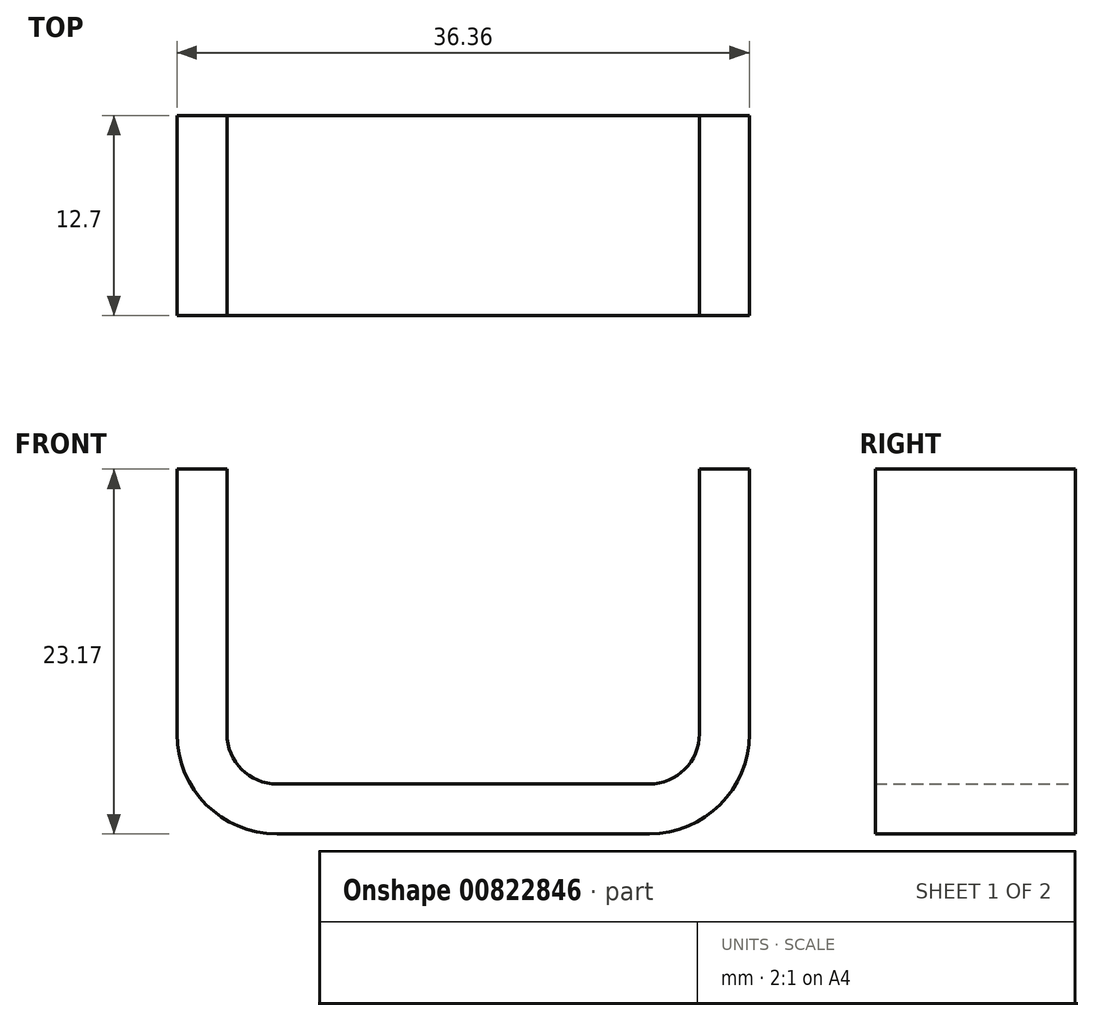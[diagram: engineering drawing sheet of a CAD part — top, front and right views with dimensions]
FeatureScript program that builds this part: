
annotation { "Feature Type Name" : "Feature", "Feature Type Description" : "" }
export const myFeature = defineFeature(function(context is Context, id is Id, definition is map)
    precondition{}
    {
        {
            var Q0;
            Q0=qCreatedBy(makeId("Front.planeOp"),FACE);
            var sketch = newSketch(context, id + "F0", { "sketchPlane" : qUnion([Q0])});
            skLineSegment(sketch, "E0", {"start": v(0, 0) * mm, "end": v(0, 17.47) * mm, "construction": true});
            skLineSegment(sketch, "E1", {"start": v(0, 0) * mm, "end": v(-15, 0) * mm});
            skLineSegment(sketch, "E2", {"start": v(-15, 0) * mm, "end": v(-15, 20) * mm});
            skLineSegment(sketch, "E3.MirrorCS", {"start": v(0, 0) * mm, "end": v(15, 0) * mm});
            skLineSegment(sketch, "E4.MirrorCS", {"start": v(15, 0) * mm, "end": v(15, 20) * mm});
            skLineSegment(sketch, "E5.0", {"start": v(-18.18, -3.18) * mm, "end": v(-18.18, 20) * mm});
            skLineSegment(sketch, "E5.1", {"start": v(0, -3.17) * mm, "end": v(-18.18, -3.18) * mm});
            skLineSegment(sketch, "E5.2", {"start": v(0, -3.17) * mm, "end": v(18.18, -3.17) * mm});
            skLineSegment(sketch, "E5.3", {"start": v(18.18, -3.18) * mm, "end": v(18.18, 20) * mm});
            skLineSegment(sketch, "E6", {"start": v(-18.18, 20) * mm, "end": v(-15, 20) * mm});
            skLineSegment(sketch, "E7", {"start": v(15, 20) * mm, "end": v(18.18, 20) * mm});
            skSolve(sketch);
        }
        {
            var Q0;
            Q0 = qSketchRegion(id + "F0", true);
            extrude(context, id + "F1", {"entities" : qUnion([Q0]), "endBound" : BoundingType.SYMMETRIC, "depth" : 12.7 * mm, "offsetDistance" : 25 * mm});
        }
        {
            var Q0;
            Q0=makeQuery(id+"F1.opExtrude","SWEPT_EDGE",EDGE,{"disambiguationData":[OSD([sQuery(id+"F0.wireOp",EDGE,"E3.MirrorCS"),sQuery(id+"F0.wireOp",EDGE,"E4.MirrorCS")])]});
            var Q1;
            Q1=makeQuery(id+"F1.opExtrude","SWEPT_EDGE",EDGE,{"disambiguationData":[OSD([sQuery(id+"F0.wireOp",EDGE,"E1"),sQuery(id+"F0.wireOp",EDGE,"E2")])]});
            fillet(context, id + "F2", {"entities" : qUnion([Q0, Q1]), "radius" : (25.4 / 8) * mm, "tangentPropagation" : true, "allowEdgeOverflow" : false});
        }
        {
            var Q0;
            Q0=makeQuery(id+"F1.opExtrude","SWEPT_EDGE",EDGE,{"disambiguationData":[OSD([sQuery(id+"F0.wireOp",EDGE,"E5.0"),sQuery(id+"F0.wireOp",EDGE,"E5.1")])]});
            var Q1;
            Q1=makeQuery(id+"F1.opExtrude","SWEPT_EDGE",EDGE,{"disambiguationData":[OSD([sQuery(id+"F0.wireOp",EDGE,"E5.2"),sQuery(id+"F0.wireOp",EDGE,"E5.3")])]});
            fillet(context, id + "F3", {"entities" : qUnion([Q0, Q1]), "radius" : ((25.4 / 8) * 2) * mm, "tangentPropagation" : true, "allowEdgeOverflow" : false});
        }
    });
